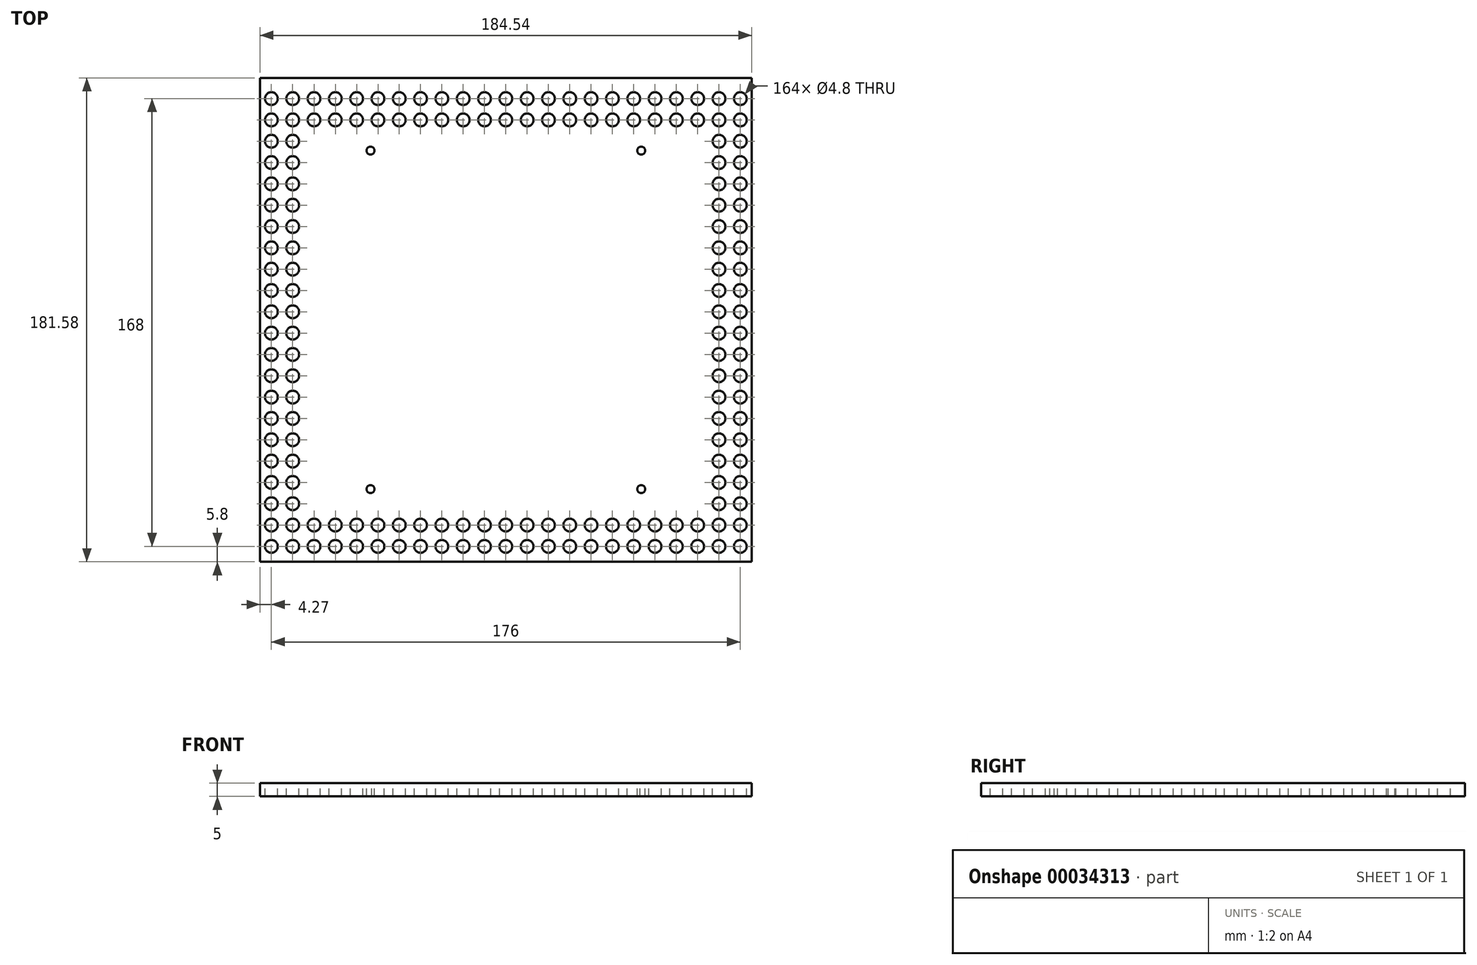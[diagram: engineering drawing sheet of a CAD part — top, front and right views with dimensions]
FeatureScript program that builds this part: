
annotation { "Feature Type Name" : "Feature", "Feature Type Description" : "" }
export const myFeature = defineFeature(function(context is Context, id is Id, definition is map)
    precondition{}
    {
        {
            var Q0;
            Q0=qCreatedBy(makeId("Top.planeOp"),FACE);
            var sketch = newSketch(context, id + "F0", { "sketchPlane" : qUnion([Q0])});
            skLineSegment(sketch, "E0.rect.bottom", {"start": v(92.28, 90.8) * mm, "end": v(-92.27, 90.8) * mm});
            skLineSegment(sketch, "E0.rect.top", {"start": v(92.27, -90.8) * mm, "end": v(-92.28, -90.8) * mm});
            skLineSegment(sketch, "E0.rect.left", {"start": v(92.28, 90.8) * mm, "end": v(92.27, -90.8) * mm});
            skLineSegment(sketch, "E0.rect.right", {"start": v(-92.27, 90.8) * mm, "end": v(-92.28, -90.8) * mm});
            skPoint(sketch, "E0.rect.middle", {"position": v(0, 0) * mm});
            skSolve(sketch);
        }
        {
            var Q0;
            Q0 = qSketchRegion(id + "F0", true);
            extrude(context, id + "F1", {"entities" : qUnion([Q0]), "depth" : 5 * mm});
        }
        {
            var Q0;
            Q0=makeQuery(id+"F1.opExtrude","CAP_FACE",FACE,{"disambiguationData":[OSD([sQuery(id+"F0.wireOp",EDGE,"E0.rect.bottom"),sQuery(id+"F0.wireOp",EDGE,"E0.rect.top"),sQuery(id+"F0.wireOp",EDGE,"E0.rect.left"),sQuery(id+"F0.wireOp",EDGE,"E0.rect.right")])],"isStart":false});
            var sketch = newSketch(context, id + "F2", { "sketchPlane" : qUnion([Q0])});
            skCircle(sketch, "E1", {"center": v(-88, -85) * mm, "radius": 2.4 * mm});
            skCircle(sketch, "E2.0.1.0", {"center": v(-88, -77) * mm, "radius": 2.4 * mm});
            skCircle(sketch, "E2.1.0.0", {"center": v(-80, -85) * mm, "radius": 2.4 * mm});
            skCircle(sketch, "E2.1.1.0", {"center": v(-80, -77) * mm, "radius": 2.4 * mm});
            skCircle(sketch, "E2.2.0.0", {"center": v(-72, -85) * mm, "radius": 2.4 * mm});
            skCircle(sketch, "E2.2.1.0", {"center": v(-72, -77) * mm, "radius": 2.4 * mm});
            skCircle(sketch, "E2.3.0.0", {"center": v(-64, -85) * mm, "radius": 2.4 * mm});
            skCircle(sketch, "E2.3.1.0", {"center": v(-64, -77) * mm, "radius": 2.4 * mm});
            skCircle(sketch, "E2.4.0.0", {"center": v(-56, -85) * mm, "radius": 2.4 * mm});
            skCircle(sketch, "E2.4.1.0", {"center": v(-56, -77) * mm, "radius": 2.4 * mm});
            skCircle(sketch, "E2.5.0.0", {"center": v(-48, -85) * mm, "radius": 2.4 * mm});
            skCircle(sketch, "E2.5.1.0", {"center": v(-48, -77) * mm, "radius": 2.4 * mm});
            skCircle(sketch, "E2.6.0.0", {"center": v(-40, -85) * mm, "radius": 2.4 * mm});
            skCircle(sketch, "E2.6.1.0", {"center": v(-40, -77) * mm, "radius": 2.4 * mm});
            skCircle(sketch, "E2.7.0.0", {"center": v(-32, -85) * mm, "radius": 2.4 * mm});
            skCircle(sketch, "E2.7.1.0", {"center": v(-32, -77) * mm, "radius": 2.4 * mm});
            skCircle(sketch, "E2.8.0.0", {"center": v(-24, -85) * mm, "radius": 2.4 * mm});
            skCircle(sketch, "E2.8.1.0", {"center": v(-24, -77) * mm, "radius": 2.4 * mm});
            skCircle(sketch, "E2.9.0.0", {"center": v(-16, -85) * mm, "radius": 2.4 * mm});
            skCircle(sketch, "E2.9.1.0", {"center": v(-16, -77) * mm, "radius": 2.4 * mm});
            skCircle(sketch, "E2.10.0.0", {"center": v(-8, -85) * mm, "radius": 2.4 * mm});
            skCircle(sketch, "E2.10.1.0", {"center": v(-8, -77) * mm, "radius": 2.4 * mm});
            skCircle(sketch, "E2.11.0.0", {"center": v(0, -85) * mm, "radius": 2.4 * mm});
            skCircle(sketch, "E2.11.1.0", {"center": v(0, -77) * mm, "radius": 2.4 * mm});
            skCircle(sketch, "E2.12.0.0", {"center": v(8, -85) * mm, "radius": 2.4 * mm});
            skCircle(sketch, "E2.12.1.0", {"center": v(8, -77) * mm, "radius": 2.4 * mm});
            skCircle(sketch, "E2.13.0.0", {"center": v(16, -85) * mm, "radius": 2.4 * mm});
            skCircle(sketch, "E2.13.1.0", {"center": v(16, -77) * mm, "radius": 2.4 * mm});
            skCircle(sketch, "E2.14.0.0", {"center": v(24, -85) * mm, "radius": 2.4 * mm});
            skCircle(sketch, "E2.14.1.0", {"center": v(24, -77) * mm, "radius": 2.4 * mm});
            skCircle(sketch, "E2.15.0.0", {"center": v(32, -85) * mm, "radius": 2.4 * mm});
            skCircle(sketch, "E2.15.1.0", {"center": v(32, -77) * mm, "radius": 2.4 * mm});
            skCircle(sketch, "E2.16.0.0", {"center": v(40, -85) * mm, "radius": 2.4 * mm});
            skCircle(sketch, "E2.16.1.0", {"center": v(40, -77) * mm, "radius": 2.4 * mm});
            skCircle(sketch, "E2.17.0.0", {"center": v(48, -85) * mm, "radius": 2.4 * mm});
            skCircle(sketch, "E2.17.1.0", {"center": v(48, -77) * mm, "radius": 2.4 * mm});
            skCircle(sketch, "E2.18.0.0", {"center": v(56, -85) * mm, "radius": 2.4 * mm});
            skCircle(sketch, "E2.18.1.0", {"center": v(56, -77) * mm, "radius": 2.4 * mm});
            skCircle(sketch, "E2.19.0.0", {"center": v(64, -85) * mm, "radius": 2.4 * mm});
            skCircle(sketch, "E2.19.1.0", {"center": v(64, -77) * mm, "radius": 2.4 * mm});
            skCircle(sketch, "E2.20.0.0", {"center": v(72, -85) * mm, "radius": 2.4 * mm});
            skCircle(sketch, "E2.20.1.0", {"center": v(72, -77) * mm, "radius": 2.4 * mm});
            skCircle(sketch, "E2.21.0.0", {"center": v(80, -85) * mm, "radius": 2.4 * mm});
            skCircle(sketch, "E2.21.1.0", {"center": v(80, -77) * mm, "radius": 2.4 * mm});
            skCircle(sketch, "E2.22.0.0", {"center": v(88, -85) * mm, "radius": 2.4 * mm});
            skCircle(sketch, "E2.22.1.0", {"center": v(88, -77) * mm, "radius": 2.4 * mm});
            skLineSegment(sketch, "E2.direction1", {"start": v(-88, -85) * mm, "end": v(-80, -85) * mm, "construction": true});
            skLineSegment(sketch, "E2.direction2", {"start": v(-88, -85) * mm, "end": v(-88, -77) * mm, "construction": true});
            skCircle(sketch, "E3.0.1.0", {"center": v(-88, -68.99) * mm, "radius": 2.4 * mm});
            skCircle(sketch, "E3.0.2.0", {"center": v(-88, -60.99) * mm, "radius": 2.4 * mm});
            skCircle(sketch, "E3.0.3.0", {"center": v(-88, -52.99) * mm, "radius": 2.4 * mm});
            skCircle(sketch, "E3.0.4.0", {"center": v(-88, -44.99) * mm, "radius": 2.4 * mm});
            skCircle(sketch, "E3.0.5.0", {"center": v(-88, -36.99) * mm, "radius": 2.4 * mm});
            skCircle(sketch, "E3.0.6.0", {"center": v(-88, -28.99) * mm, "radius": 2.4 * mm});
            skCircle(sketch, "E3.0.7.0", {"center": v(-88, -20.99) * mm, "radius": 2.4 * mm});
            skCircle(sketch, "E3.0.8.0", {"center": v(-88, -12.99) * mm, "radius": 2.4 * mm});
            skCircle(sketch, "E3.0.9.0", {"center": v(-88, -4.99) * mm, "radius": 2.4 * mm});
            skCircle(sketch, "E3.0.10.0", {"center": v(-88, 3.01) * mm, "radius": 2.4 * mm});
            skCircle(sketch, "E3.0.11.0", {"center": v(-88, 11.01) * mm, "radius": 2.4 * mm});
            skCircle(sketch, "E3.0.12.0", {"center": v(-88, 19.01) * mm, "radius": 2.4 * mm});
            skCircle(sketch, "E3.0.13.0", {"center": v(-88, 27.01) * mm, "radius": 2.4 * mm});
            skCircle(sketch, "E3.0.14.0", {"center": v(-88, 35.01) * mm, "radius": 2.4 * mm});
            skCircle(sketch, "E3.0.15.0", {"center": v(-88, 43.01) * mm, "radius": 2.4 * mm});
            skCircle(sketch, "E3.0.16.0", {"center": v(-88, 51.01) * mm, "radius": 2.4 * mm});
            skCircle(sketch, "E3.0.17.0", {"center": v(-88, 59.01) * mm, "radius": 2.4 * mm});
            skCircle(sketch, "E3.0.18.0", {"center": v(-88, 67.01) * mm, "radius": 2.4 * mm});
            skCircle(sketch, "E3.0.19.0", {"center": v(-88, 75.01) * mm, "radius": 2.4 * mm});
            skCircle(sketch, "E3.0.20.0", {"center": v(-88, 83.01) * mm, "radius": 2.4 * mm});
            skCircle(sketch, "E3.1.1.0", {"center": v(-80, -68.99) * mm, "radius": 2.4 * mm});
            skCircle(sketch, "E3.1.2.0", {"center": v(-80, -60.99) * mm, "radius": 2.4 * mm});
            skCircle(sketch, "E3.1.3.0", {"center": v(-80, -52.99) * mm, "radius": 2.4 * mm});
            skCircle(sketch, "E3.1.4.0", {"center": v(-80, -44.99) * mm, "radius": 2.4 * mm});
            skCircle(sketch, "E3.1.5.0", {"center": v(-80, -36.99) * mm, "radius": 2.4 * mm});
            skCircle(sketch, "E3.1.6.0", {"center": v(-80, -28.99) * mm, "radius": 2.4 * mm});
            skCircle(sketch, "E3.1.7.0", {"center": v(-80, -20.99) * mm, "radius": 2.4 * mm});
            skCircle(sketch, "E3.1.8.0", {"center": v(-80, -12.99) * mm, "radius": 2.4 * mm});
            skCircle(sketch, "E3.1.9.0", {"center": v(-80, -4.99) * mm, "radius": 2.4 * mm});
            skCircle(sketch, "E3.1.10.0", {"center": v(-80, 3.01) * mm, "radius": 2.4 * mm});
            skCircle(sketch, "E3.1.11.0", {"center": v(-80, 11.01) * mm, "radius": 2.4 * mm});
            skCircle(sketch, "E3.1.12.0", {"center": v(-80, 19.01) * mm, "radius": 2.4 * mm});
            skCircle(sketch, "E3.1.13.0", {"center": v(-80, 27.01) * mm, "radius": 2.4 * mm});
            skCircle(sketch, "E3.1.14.0", {"center": v(-80, 35.01) * mm, "radius": 2.4 * mm});
            skCircle(sketch, "E3.1.15.0", {"center": v(-80, 43.01) * mm, "radius": 2.4 * mm});
            skCircle(sketch, "E3.1.16.0", {"center": v(-80, 51.01) * mm, "radius": 2.4 * mm});
            skCircle(sketch, "E3.1.17.0", {"center": v(-80, 59.01) * mm, "radius": 2.4 * mm});
            skCircle(sketch, "E3.1.18.0", {"center": v(-80, 67.01) * mm, "radius": 2.4 * mm});
            skCircle(sketch, "E3.1.19.0", {"center": v(-80, 75.01) * mm, "radius": 2.4 * mm});
            skCircle(sketch, "E3.1.20.0", {"center": v(-80, 83.01) * mm, "radius": 2.4 * mm});
            skLineSegment(sketch, "E3.direction1", {"start": v(-88, -77) * mm, "end": v(-80, -77) * mm, "construction": true});
            skLineSegment(sketch, "E3.direction2", {"start": v(-88, -77) * mm, "end": v(-88, -68.99) * mm, "construction": true});
            skCircle(sketch, "E4.2.0.0", {"center": v(-72, 75.01) * mm, "radius": 2.4 * mm});
            skCircle(sketch, "E4.2.1.0", {"center": v(-72, 83.01) * mm, "radius": 2.4 * mm});
            skCircle(sketch, "E4.3.0.0", {"center": v(-64, 75.01) * mm, "radius": 2.4 * mm});
            skCircle(sketch, "E4.3.1.0", {"center": v(-64, 83.01) * mm, "radius": 2.4 * mm});
            skCircle(sketch, "E4.4.0.0", {"center": v(-56, 75.01) * mm, "radius": 2.4 * mm});
            skCircle(sketch, "E4.4.1.0", {"center": v(-56, 83.01) * mm, "radius": 2.4 * mm});
            skCircle(sketch, "E4.5.0.0", {"center": v(-48, 75.01) * mm, "radius": 2.4 * mm});
            skCircle(sketch, "E4.5.1.0", {"center": v(-48, 83.01) * mm, "radius": 2.4 * mm});
            skCircle(sketch, "E4.6.0.0", {"center": v(-40, 75.01) * mm, "radius": 2.4 * mm});
            skCircle(sketch, "E4.6.1.0", {"center": v(-40, 83.01) * mm, "radius": 2.4 * mm});
            skCircle(sketch, "E4.7.0.0", {"center": v(-32, 75.01) * mm, "radius": 2.4 * mm});
            skCircle(sketch, "E4.7.1.0", {"center": v(-32, 83.01) * mm, "radius": 2.4 * mm});
            skCircle(sketch, "E4.8.0.0", {"center": v(-24, 75.01) * mm, "radius": 2.4 * mm});
            skCircle(sketch, "E4.8.1.0", {"center": v(-24, 83.01) * mm, "radius": 2.4 * mm});
            skCircle(sketch, "E4.9.0.0", {"center": v(-16, 75.01) * mm, "radius": 2.4 * mm});
            skCircle(sketch, "E4.9.1.0", {"center": v(-16, 83.01) * mm, "radius": 2.4 * mm});
            skCircle(sketch, "E4.10.0.0", {"center": v(-8, 75.01) * mm, "radius": 2.4 * mm});
            skCircle(sketch, "E4.10.1.0", {"center": v(-8, 83.01) * mm, "radius": 2.4 * mm});
            skCircle(sketch, "E4.11.0.0", {"center": v(0, 75.01) * mm, "radius": 2.4 * mm});
            skCircle(sketch, "E4.11.1.0", {"center": v(0, 83.01) * mm, "radius": 2.4 * mm});
            skCircle(sketch, "E4.12.0.0", {"center": v(8, 75.01) * mm, "radius": 2.4 * mm});
            skCircle(sketch, "E4.12.1.0", {"center": v(8, 83.01) * mm, "radius": 2.4 * mm});
            skCircle(sketch, "E4.13.0.0", {"center": v(16, 75.01) * mm, "radius": 2.4 * mm});
            skCircle(sketch, "E4.13.1.0", {"center": v(16, 83.01) * mm, "radius": 2.4 * mm});
            skCircle(sketch, "E4.14.0.0", {"center": v(24, 75.01) * mm, "radius": 2.4 * mm});
            skCircle(sketch, "E4.14.1.0", {"center": v(24, 83.01) * mm, "radius": 2.4 * mm});
            skCircle(sketch, "E4.15.0.0", {"center": v(32, 75.01) * mm, "radius": 2.4 * mm});
            skCircle(sketch, "E4.15.1.0", {"center": v(32, 83.01) * mm, "radius": 2.4 * mm});
            skCircle(sketch, "E4.16.0.0", {"center": v(40, 75.01) * mm, "radius": 2.4 * mm});
            skCircle(sketch, "E4.16.1.0", {"center": v(40, 83.01) * mm, "radius": 2.4 * mm});
            skCircle(sketch, "E4.17.0.0", {"center": v(48, 75.01) * mm, "radius": 2.4 * mm});
            skCircle(sketch, "E4.17.1.0", {"center": v(48, 83.01) * mm, "radius": 2.4 * mm});
            skCircle(sketch, "E4.18.0.0", {"center": v(56, 75.01) * mm, "radius": 2.4 * mm});
            skCircle(sketch, "E4.18.1.0", {"center": v(56, 83.01) * mm, "radius": 2.4 * mm});
            skCircle(sketch, "E4.19.0.0", {"center": v(64, 75.01) * mm, "radius": 2.4 * mm});
            skCircle(sketch, "E4.19.1.0", {"center": v(64, 83.01) * mm, "radius": 2.4 * mm});
            skCircle(sketch, "E4.20.0.0", {"center": v(72, 75.01) * mm, "radius": 2.4 * mm});
            skCircle(sketch, "E4.20.1.0", {"center": v(72, 83.01) * mm, "radius": 2.4 * mm});
            skCircle(sketch, "E4.21.0.0", {"center": v(80, 75.01) * mm, "radius": 2.4 * mm});
            skCircle(sketch, "E4.21.1.0", {"center": v(80, 83.01) * mm, "radius": 2.4 * mm});
            skCircle(sketch, "E4.22.0.0", {"center": v(88, 75.01) * mm, "radius": 2.4 * mm});
            skCircle(sketch, "E4.22.1.0", {"center": v(88, 83.01) * mm, "radius": 2.4 * mm});
            skLineSegment(sketch, "E4.direction1", {"start": v(-88, 75.01) * mm, "end": v(-80, 75.01) * mm, "construction": true});
            skLineSegment(sketch, "E4.direction2", {"start": v(-88, 75.01) * mm, "end": v(-88, 83.01) * mm, "construction": true});
            skCircle(sketch, "E5.0.2.0", {"center": v(80, -68.99) * mm, "radius": 2.4 * mm});
            skCircle(sketch, "E5.0.3.0", {"center": v(80, -60.99) * mm, "radius": 2.4 * mm});
            skCircle(sketch, "E5.0.4.0", {"center": v(80, -52.99) * mm, "radius": 2.4 * mm});
            skCircle(sketch, "E5.0.5.0", {"center": v(80, -44.99) * mm, "radius": 2.4 * mm});
            skCircle(sketch, "E5.0.6.0", {"center": v(80, -36.99) * mm, "radius": 2.4 * mm});
            skCircle(sketch, "E5.0.7.0", {"center": v(80, -28.99) * mm, "radius": 2.4 * mm});
            skCircle(sketch, "E5.0.8.0", {"center": v(80, -20.99) * mm, "radius": 2.4 * mm});
            skCircle(sketch, "E5.0.9.0", {"center": v(80, -12.99) * mm, "radius": 2.4 * mm});
            skCircle(sketch, "E5.0.10.0", {"center": v(80, -4.99) * mm, "radius": 2.4 * mm});
            skCircle(sketch, "E5.0.11.0", {"center": v(80, 3.01) * mm, "radius": 2.4 * mm});
            skCircle(sketch, "E5.0.12.0", {"center": v(80, 11.01) * mm, "radius": 2.4 * mm});
            skCircle(sketch, "E5.0.13.0", {"center": v(80, 19.01) * mm, "radius": 2.4 * mm});
            skCircle(sketch, "E5.0.14.0", {"center": v(80, 27.01) * mm, "radius": 2.4 * mm});
            skCircle(sketch, "E5.0.15.0", {"center": v(80, 35.01) * mm, "radius": 2.4 * mm});
            skCircle(sketch, "E5.0.16.0", {"center": v(80, 43.01) * mm, "radius": 2.4 * mm});
            skCircle(sketch, "E5.0.17.0", {"center": v(80, 51.01) * mm, "radius": 2.4 * mm});
            skCircle(sketch, "E5.0.18.0", {"center": v(80, 59.01) * mm, "radius": 2.4 * mm});
            skCircle(sketch, "E5.0.19.0", {"center": v(80, 67.01) * mm, "radius": 2.4 * mm});
            skCircle(sketch, "E5.1.2.0", {"center": v(88, -68.99) * mm, "radius": 2.4 * mm});
            skCircle(sketch, "E5.1.3.0", {"center": v(88, -60.99) * mm, "radius": 2.4 * mm});
            skCircle(sketch, "E5.1.4.0", {"center": v(88, -52.99) * mm, "radius": 2.4 * mm});
            skCircle(sketch, "E5.1.5.0", {"center": v(88, -44.99) * mm, "radius": 2.4 * mm});
            skCircle(sketch, "E5.1.6.0", {"center": v(88, -36.99) * mm, "radius": 2.4 * mm});
            skCircle(sketch, "E5.1.7.0", {"center": v(88, -28.99) * mm, "radius": 2.4 * mm});
            skCircle(sketch, "E5.1.8.0", {"center": v(88, -20.99) * mm, "radius": 2.4 * mm});
            skCircle(sketch, "E5.1.9.0", {"center": v(88, -12.99) * mm, "radius": 2.4 * mm});
            skCircle(sketch, "E5.1.10.0", {"center": v(88, -4.99) * mm, "radius": 2.4 * mm});
            skCircle(sketch, "E5.1.11.0", {"center": v(88, 3.01) * mm, "radius": 2.4 * mm});
            skCircle(sketch, "E5.1.12.0", {"center": v(88, 11.01) * mm, "radius": 2.4 * mm});
            skCircle(sketch, "E5.1.13.0", {"center": v(88, 19.01) * mm, "radius": 2.4 * mm});
            skCircle(sketch, "E5.1.14.0", {"center": v(88, 27.01) * mm, "radius": 2.4 * mm});
            skCircle(sketch, "E5.1.15.0", {"center": v(88, 35.01) * mm, "radius": 2.4 * mm});
            skCircle(sketch, "E5.1.16.0", {"center": v(88, 43.01) * mm, "radius": 2.4 * mm});
            skCircle(sketch, "E5.1.17.0", {"center": v(88, 51.01) * mm, "radius": 2.4 * mm});
            skCircle(sketch, "E5.1.18.0", {"center": v(88, 59.01) * mm, "radius": 2.4 * mm});
            skCircle(sketch, "E5.1.19.0", {"center": v(88, 67.01) * mm, "radius": 2.4 * mm});
            skLineSegment(sketch, "E5.direction1", {"start": v(80, -85) * mm, "end": v(88, -85) * mm, "construction": true});
            skLineSegment(sketch, "E5.direction2", {"start": v(80, -85) * mm, "end": v(80, -77) * mm, "construction": true});
            skSolve(sketch);
        }
        {
            var Q0;
            Q0=makeQuery(id+"F2.imprint","IMPRINT",FACE,{"disambiguationData":[TD([[makeQuery(id+"F2.imprint","IMPRINT",EDGE,{"derivedFrom":sQuery(id+"F2.wireOp",EDGE,"E2.21.1.0")}),1.0]])]});
            var Q1;
            Q1=makeQuery(id+"F2.imprint","IMPRINT",FACE,{"disambiguationData":[TD([[makeQuery(id+"F2.imprint","IMPRINT",EDGE,{"derivedFrom":sQuery(id+"F2.wireOp",EDGE,"E2.22.1.0")}),1.0]])]});
            var Q2;
            Q2=makeQuery(id+"F2.imprint","IMPRINT",FACE,{"disambiguationData":[TD([[makeQuery(id+"F2.imprint","IMPRINT",EDGE,{"derivedFrom":sQuery(id+"F2.wireOp",EDGE,"E2.22.0.0")}),1.0]])]});
            var Q3;
            Q3=makeQuery(id+"F2.imprint","IMPRINT",FACE,{"disambiguationData":[TD([[makeQuery(id+"F2.imprint","IMPRINT",EDGE,{"derivedFrom":sQuery(id+"F2.wireOp",EDGE,"E2.21.0.0")}),1.0]])]});
            var Q4;
            Q4=makeQuery(id+"F2.imprint","IMPRINT",FACE,{"disambiguationData":[TD([[makeQuery(id+"F2.imprint","IMPRINT",EDGE,{"derivedFrom":sQuery(id+"F2.wireOp",EDGE,"E2.20.1.0")}),1.0]])]});
            var Q5;
            Q5=makeQuery(id+"F2.imprint","IMPRINT",FACE,{"disambiguationData":[TD([[makeQuery(id+"F2.imprint","IMPRINT",EDGE,{"derivedFrom":sQuery(id+"F2.wireOp",EDGE,"E2.20.0.0")}),1.0]])]});
            var Q6;
            Q6=makeQuery(id+"F2.imprint","IMPRINT",FACE,{"disambiguationData":[TD([[makeQuery(id+"F2.imprint","IMPRINT",EDGE,{"derivedFrom":sQuery(id+"F2.wireOp",EDGE,"E2.19.0.0")}),1.0]])]});
            var Q7;
            Q7=makeQuery(id+"F2.imprint","IMPRINT",FACE,{"disambiguationData":[TD([[makeQuery(id+"F2.imprint","IMPRINT",EDGE,{"derivedFrom":sQuery(id+"F2.wireOp",EDGE,"E2.19.1.0")}),1.0]])]});
            var Q8;
            Q8=makeQuery(id+"F2.imprint","IMPRINT",FACE,{"disambiguationData":[TD([[makeQuery(id+"F2.imprint","IMPRINT",EDGE,{"derivedFrom":sQuery(id+"F2.wireOp",EDGE,"E2.18.1.0")}),1.0]])]});
            var Q9;
            Q9=makeQuery(id+"F2.imprint","IMPRINT",FACE,{"disambiguationData":[TD([[makeQuery(id+"F2.imprint","IMPRINT",EDGE,{"derivedFrom":sQuery(id+"F2.wireOp",EDGE,"E2.18.0.0")}),1.0]])]});
            var Q10;
            Q10=makeQuery(id+"F2.imprint","IMPRINT",FACE,{"disambiguationData":[TD([[makeQuery(id+"F2.imprint","IMPRINT",EDGE,{"derivedFrom":sQuery(id+"F2.wireOp",EDGE,"E2.17.0.0")}),1.0]])]});
            var Q11;
            Q11=makeQuery(id+"F2.imprint","IMPRINT",FACE,{"disambiguationData":[TD([[makeQuery(id+"F2.imprint","IMPRINT",EDGE,{"derivedFrom":sQuery(id+"F2.wireOp",EDGE,"E2.17.1.0")}),1.0]])]});
            var Q12;
            Q12=makeQuery(id+"F2.imprint","IMPRINT",FACE,{"disambiguationData":[TD([[makeQuery(id+"F2.imprint","IMPRINT",EDGE,{"derivedFrom":sQuery(id+"F2.wireOp",EDGE,"E2.16.1.0")}),1.0]])]});
            var Q13;
            Q13=makeQuery(id+"F2.imprint","IMPRINT",FACE,{"disambiguationData":[TD([[makeQuery(id+"F2.imprint","IMPRINT",EDGE,{"derivedFrom":sQuery(id+"F2.wireOp",EDGE,"E2.16.0.0")}),1.0]])]});
            var Q14;
            Q14=makeQuery(id+"F2.imprint","IMPRINT",FACE,{"disambiguationData":[TD([[makeQuery(id+"F2.imprint","IMPRINT",EDGE,{"derivedFrom":sQuery(id+"F2.wireOp",EDGE,"E2.15.0.0")}),1.0]])]});
            var Q15;
            Q15=makeQuery(id+"F2.imprint","IMPRINT",FACE,{"disambiguationData":[TD([[makeQuery(id+"F2.imprint","IMPRINT",EDGE,{"derivedFrom":sQuery(id+"F2.wireOp",EDGE,"E2.15.1.0")}),1.0]])]});
            var Q16;
            Q16=makeQuery(id+"F2.imprint","IMPRINT",FACE,{"disambiguationData":[TD([[makeQuery(id+"F2.imprint","IMPRINT",EDGE,{"derivedFrom":sQuery(id+"F2.wireOp",EDGE,"E2.14.1.0")}),1.0]])]});
            var Q17;
            Q17=makeQuery(id+"F2.imprint","IMPRINT",FACE,{"disambiguationData":[TD([[makeQuery(id+"F2.imprint","IMPRINT",EDGE,{"derivedFrom":sQuery(id+"F2.wireOp",EDGE,"E2.14.0.0")}),1.0]])]});
            var Q18;
            Q18=makeQuery(id+"F2.imprint","IMPRINT",FACE,{"disambiguationData":[TD([[makeQuery(id+"F2.imprint","IMPRINT",EDGE,{"derivedFrom":sQuery(id+"F2.wireOp",EDGE,"E2.13.0.0")}),1.0]])]});
            var Q19;
            Q19=makeQuery(id+"F2.imprint","IMPRINT",FACE,{"disambiguationData":[TD([[makeQuery(id+"F2.imprint","IMPRINT",EDGE,{"derivedFrom":sQuery(id+"F2.wireOp",EDGE,"E2.13.1.0")}),1.0]])]});
            var Q20;
            Q20=makeQuery(id+"F2.imprint","IMPRINT",FACE,{"disambiguationData":[TD([[makeQuery(id+"F2.imprint","IMPRINT",EDGE,{"derivedFrom":sQuery(id+"F2.wireOp",EDGE,"E2.12.1.0")}),1.0]])]});
            var Q21;
            Q21=makeQuery(id+"F2.imprint","IMPRINT",FACE,{"disambiguationData":[TD([[makeQuery(id+"F2.imprint","IMPRINT",EDGE,{"derivedFrom":sQuery(id+"F2.wireOp",EDGE,"E2.12.0.0")}),1.0]])]});
            var Q22;
            Q22=makeQuery(id+"F2.imprint","IMPRINT",FACE,{"disambiguationData":[TD([[makeQuery(id+"F2.imprint","IMPRINT",EDGE,{"derivedFrom":sQuery(id+"F2.wireOp",EDGE,"E2.11.0.0")}),1.0]])]});
            var Q23;
            Q23=makeQuery(id+"F2.imprint","IMPRINT",FACE,{"disambiguationData":[TD([[makeQuery(id+"F2.imprint","IMPRINT",EDGE,{"derivedFrom":sQuery(id+"F2.wireOp",EDGE,"E2.11.1.0")}),1.0]])]});
            var Q24;
            Q24=makeQuery(id+"F2.imprint","IMPRINT",FACE,{"disambiguationData":[TD([[makeQuery(id+"F2.imprint","IMPRINT",EDGE,{"derivedFrom":sQuery(id+"F2.wireOp",EDGE,"E2.10.1.0")}),1.0]])]});
            var Q25;
            Q25=makeQuery(id+"F2.imprint","IMPRINT",FACE,{"disambiguationData":[TD([[makeQuery(id+"F2.imprint","IMPRINT",EDGE,{"derivedFrom":sQuery(id+"F2.wireOp",EDGE,"E2.10.0.0")}),1.0]])]});
            var Q26;
            Q26=makeQuery(id+"F2.imprint","IMPRINT",FACE,{"disambiguationData":[TD([[makeQuery(id+"F2.imprint","IMPRINT",EDGE,{"derivedFrom":sQuery(id+"F2.wireOp",EDGE,"E2.9.0.0")}),1.0]])]});
            var Q27;
            Q27=makeQuery(id+"F2.imprint","IMPRINT",FACE,{"disambiguationData":[TD([[makeQuery(id+"F2.imprint","IMPRINT",EDGE,{"derivedFrom":sQuery(id+"F2.wireOp",EDGE,"E2.9.1.0")}),1.0]])]});
            var Q28;
            Q28=makeQuery(id+"F2.imprint","IMPRINT",FACE,{"disambiguationData":[TD([[makeQuery(id+"F2.imprint","IMPRINT",EDGE,{"derivedFrom":sQuery(id+"F2.wireOp",EDGE,"E2.8.1.0")}),1.0]])]});
            var Q29;
            Q29=makeQuery(id+"F2.imprint","IMPRINT",FACE,{"disambiguationData":[TD([[makeQuery(id+"F2.imprint","IMPRINT",EDGE,{"derivedFrom":sQuery(id+"F2.wireOp",EDGE,"E2.8.0.0")}),1.0]])]});
            var Q30;
            Q30=makeQuery(id+"F2.imprint","IMPRINT",FACE,{"disambiguationData":[TD([[makeQuery(id+"F2.imprint","IMPRINT",EDGE,{"derivedFrom":sQuery(id+"F2.wireOp",EDGE,"E2.7.0.0")}),1.0]])]});
            var Q31;
            Q31=makeQuery(id+"F2.imprint","IMPRINT",FACE,{"disambiguationData":[TD([[makeQuery(id+"F2.imprint","IMPRINT",EDGE,{"derivedFrom":sQuery(id+"F2.wireOp",EDGE,"E2.7.1.0")}),1.0]])]});
            var Q32;
            Q32=makeQuery(id+"F2.imprint","IMPRINT",FACE,{"disambiguationData":[TD([[makeQuery(id+"F2.imprint","IMPRINT",EDGE,{"derivedFrom":sQuery(id+"F2.wireOp",EDGE,"E2.6.1.0")}),1.0]])]});
            var Q33;
            Q33=makeQuery(id+"F2.imprint","IMPRINT",FACE,{"disambiguationData":[TD([[makeQuery(id+"F2.imprint","IMPRINT",EDGE,{"derivedFrom":sQuery(id+"F2.wireOp",EDGE,"E2.6.0.0")}),1.0]])]});
            var Q34;
            Q34=makeQuery(id+"F2.imprint","IMPRINT",FACE,{"disambiguationData":[TD([[makeQuery(id+"F2.imprint","IMPRINT",EDGE,{"derivedFrom":sQuery(id+"F2.wireOp",EDGE,"E2.5.0.0")}),1.0]])]});
            var Q35;
            Q35=makeQuery(id+"F2.imprint","IMPRINT",FACE,{"disambiguationData":[TD([[makeQuery(id+"F2.imprint","IMPRINT",EDGE,{"derivedFrom":sQuery(id+"F2.wireOp",EDGE,"E2.5.1.0")}),1.0]])]});
            var Q36;
            Q36=makeQuery(id+"F2.imprint","IMPRINT",FACE,{"disambiguationData":[TD([[makeQuery(id+"F2.imprint","IMPRINT",EDGE,{"derivedFrom":sQuery(id+"F2.wireOp",EDGE,"E2.4.1.0")}),1.0]])]});
            var Q37;
            Q37=makeQuery(id+"F2.imprint","IMPRINT",FACE,{"disambiguationData":[TD([[makeQuery(id+"F2.imprint","IMPRINT",EDGE,{"derivedFrom":sQuery(id+"F2.wireOp",EDGE,"E2.4.0.0")}),1.0]])]});
            var Q38;
            Q38=makeQuery(id+"F2.imprint","IMPRINT",FACE,{"disambiguationData":[TD([[makeQuery(id+"F2.imprint","IMPRINT",EDGE,{"derivedFrom":sQuery(id+"F2.wireOp",EDGE,"E2.3.0.0")}),1.0]])]});
            var Q39;
            Q39=makeQuery(id+"F2.imprint","IMPRINT",FACE,{"disambiguationData":[TD([[makeQuery(id+"F2.imprint","IMPRINT",EDGE,{"derivedFrom":sQuery(id+"F2.wireOp",EDGE,"E2.2.0.0")}),1.0]])]});
            var Q40;
            Q40=makeQuery(id+"F2.imprint","IMPRINT",FACE,{"disambiguationData":[TD([[makeQuery(id+"F2.imprint","IMPRINT",EDGE,{"derivedFrom":sQuery(id+"F2.wireOp",EDGE,"E2.2.1.0")}),1.0]])]});
            var Q41;
            Q41=makeQuery(id+"F2.imprint","IMPRINT",FACE,{"disambiguationData":[TD([[makeQuery(id+"F2.imprint","IMPRINT",EDGE,{"derivedFrom":sQuery(id+"F2.wireOp",EDGE,"E2.3.1.0")}),1.0]])]});
            var Q42;
            Q42=makeQuery(id+"F2.imprint","IMPRINT",FACE,{"disambiguationData":[TD([[makeQuery(id+"F2.imprint","IMPRINT",EDGE,{"derivedFrom":sQuery(id+"F2.wireOp",EDGE,"E2.1.0.0")}),1.0]])]});
            var Q43;
            Q43=makeQuery(id+"F2.imprint","IMPRINT",FACE,{"disambiguationData":[TD([[makeQuery(id+"F2.imprint","IMPRINT",EDGE,{"derivedFrom":sQuery(id+"F2.wireOp",EDGE,"E1")}),1.0]])]});
            var Q44;
            Q44=makeQuery(id+"F2.imprint","IMPRINT",FACE,{"disambiguationData":[TD([[makeQuery(id+"F2.imprint","IMPRINT",EDGE,{"derivedFrom":sQuery(id+"F2.wireOp",EDGE,"E2.0.1.0")}),1.0]])]});
            var Q45;
            Q45=makeQuery(id+"F2.imprint","IMPRINT",FACE,{"disambiguationData":[TD([[makeQuery(id+"F2.imprint","IMPRINT",EDGE,{"derivedFrom":sQuery(id+"F2.wireOp",EDGE,"E2.1.1.0")}),1.0]])]});
            var Q46;
            Q46=makeQuery(id+"F2.imprint","IMPRINT",FACE,{"disambiguationData":[TD([[makeQuery(id+"F2.imprint","IMPRINT",EDGE,{"derivedFrom":sQuery(id+"F2.wireOp",EDGE,"E3.1.1.0")}),1.0]])]});
            var Q47;
            Q47=makeQuery(id+"F2.imprint","IMPRINT",FACE,{"disambiguationData":[TD([[makeQuery(id+"F2.imprint","IMPRINT",EDGE,{"derivedFrom":sQuery(id+"F2.wireOp",EDGE,"E3.0.1.0")}),1.0]])]});
            var Q48;
            Q48=makeQuery(id+"F2.imprint","IMPRINT",FACE,{"disambiguationData":[TD([[makeQuery(id+"F2.imprint","IMPRINT",EDGE,{"derivedFrom":sQuery(id+"F2.wireOp",EDGE,"E3.0.2.0")}),1.0]])]});
            var Q49;
            Q49=makeQuery(id+"F2.imprint","IMPRINT",FACE,{"disambiguationData":[TD([[makeQuery(id+"F2.imprint","IMPRINT",EDGE,{"derivedFrom":sQuery(id+"F2.wireOp",EDGE,"E3.1.2.0")}),1.0]])]});
            var Q50;
            Q50=makeQuery(id+"F2.imprint","IMPRINT",FACE,{"disambiguationData":[TD([[makeQuery(id+"F2.imprint","IMPRINT",EDGE,{"derivedFrom":sQuery(id+"F2.wireOp",EDGE,"E3.1.3.0")}),1.0]])]});
            var Q51;
            Q51=makeQuery(id+"F2.imprint","IMPRINT",FACE,{"disambiguationData":[TD([[makeQuery(id+"F2.imprint","IMPRINT",EDGE,{"derivedFrom":sQuery(id+"F2.wireOp",EDGE,"E3.0.3.0")}),1.0]])]});
            var Q52;
            Q52=makeQuery(id+"F2.imprint","IMPRINT",FACE,{"disambiguationData":[TD([[makeQuery(id+"F2.imprint","IMPRINT",EDGE,{"derivedFrom":sQuery(id+"F2.wireOp",EDGE,"E3.0.4.0")}),1.0]])]});
            var Q53;
            Q53=makeQuery(id+"F2.imprint","IMPRINT",FACE,{"disambiguationData":[TD([[makeQuery(id+"F2.imprint","IMPRINT",EDGE,{"derivedFrom":sQuery(id+"F2.wireOp",EDGE,"E3.1.4.0")}),1.0]])]});
            var Q54;
            Q54=makeQuery(id+"F2.imprint","IMPRINT",FACE,{"disambiguationData":[TD([[makeQuery(id+"F2.imprint","IMPRINT",EDGE,{"derivedFrom":sQuery(id+"F2.wireOp",EDGE,"E3.1.5.0")}),1.0]])]});
            var Q55;
            Q55=makeQuery(id+"F2.imprint","IMPRINT",FACE,{"disambiguationData":[TD([[makeQuery(id+"F2.imprint","IMPRINT",EDGE,{"derivedFrom":sQuery(id+"F2.wireOp",EDGE,"E3.0.5.0")}),1.0]])]});
            var Q56;
            Q56=makeQuery(id+"F2.imprint","IMPRINT",FACE,{"disambiguationData":[TD([[makeQuery(id+"F2.imprint","IMPRINT",EDGE,{"derivedFrom":sQuery(id+"F2.wireOp",EDGE,"E3.0.6.0")}),1.0]])]});
            var Q57;
            Q57=makeQuery(id+"F2.imprint","IMPRINT",FACE,{"disambiguationData":[TD([[makeQuery(id+"F2.imprint","IMPRINT",EDGE,{"derivedFrom":sQuery(id+"F2.wireOp",EDGE,"E3.1.6.0")}),1.0]])]});
            var Q58;
            Q58=makeQuery(id+"F2.imprint","IMPRINT",FACE,{"disambiguationData":[TD([[makeQuery(id+"F2.imprint","IMPRINT",EDGE,{"derivedFrom":sQuery(id+"F2.wireOp",EDGE,"E3.1.7.0")}),1.0]])]});
            var Q59;
            Q59=makeQuery(id+"F2.imprint","IMPRINT",FACE,{"disambiguationData":[TD([[makeQuery(id+"F2.imprint","IMPRINT",EDGE,{"derivedFrom":sQuery(id+"F2.wireOp",EDGE,"E3.0.7.0")}),1.0]])]});
            var Q60;
            Q60=makeQuery(id+"F2.imprint","IMPRINT",FACE,{"disambiguationData":[TD([[makeQuery(id+"F2.imprint","IMPRINT",EDGE,{"derivedFrom":sQuery(id+"F2.wireOp",EDGE,"E3.0.8.0")}),1.0]])]});
            var Q61;
            Q61=makeQuery(id+"F2.imprint","IMPRINT",FACE,{"disambiguationData":[TD([[makeQuery(id+"F2.imprint","IMPRINT",EDGE,{"derivedFrom":sQuery(id+"F2.wireOp",EDGE,"E3.1.8.0")}),1.0]])]});
            var Q62;
            Q62=makeQuery(id+"F2.imprint","IMPRINT",FACE,{"disambiguationData":[TD([[makeQuery(id+"F2.imprint","IMPRINT",EDGE,{"derivedFrom":sQuery(id+"F2.wireOp",EDGE,"E3.1.9.0")}),1.0]])]});
            var Q63;
            Q63=makeQuery(id+"F2.imprint","IMPRINT",FACE,{"disambiguationData":[TD([[makeQuery(id+"F2.imprint","IMPRINT",EDGE,{"derivedFrom":sQuery(id+"F2.wireOp",EDGE,"E3.0.9.0")}),1.0]])]});
            var Q64;
            Q64=makeQuery(id+"F2.imprint","IMPRINT",FACE,{"disambiguationData":[TD([[makeQuery(id+"F2.imprint","IMPRINT",EDGE,{"derivedFrom":sQuery(id+"F2.wireOp",EDGE,"E3.0.10.0")}),1.0]])]});
            var Q65;
            Q65=makeQuery(id+"F2.imprint","IMPRINT",FACE,{"disambiguationData":[TD([[makeQuery(id+"F2.imprint","IMPRINT",EDGE,{"derivedFrom":sQuery(id+"F2.wireOp",EDGE,"E3.1.10.0")}),1.0]])]});
            var Q66;
            Q66=makeQuery(id+"F2.imprint","IMPRINT",FACE,{"disambiguationData":[TD([[makeQuery(id+"F2.imprint","IMPRINT",EDGE,{"derivedFrom":sQuery(id+"F2.wireOp",EDGE,"E3.1.11.0")}),1.0]])]});
            var Q67;
            Q67=makeQuery(id+"F2.imprint","IMPRINT",FACE,{"disambiguationData":[TD([[makeQuery(id+"F2.imprint","IMPRINT",EDGE,{"derivedFrom":sQuery(id+"F2.wireOp",EDGE,"E3.0.11.0")}),1.0]])]});
            var Q68;
            Q68=makeQuery(id+"F2.imprint","IMPRINT",FACE,{"disambiguationData":[TD([[makeQuery(id+"F2.imprint","IMPRINT",EDGE,{"derivedFrom":sQuery(id+"F2.wireOp",EDGE,"E3.0.12.0")}),1.0]])]});
            var Q69;
            Q69=makeQuery(id+"F2.imprint","IMPRINT",FACE,{"disambiguationData":[TD([[makeQuery(id+"F2.imprint","IMPRINT",EDGE,{"derivedFrom":sQuery(id+"F2.wireOp",EDGE,"E3.1.12.0")}),1.0]])]});
            var Q70;
            Q70=makeQuery(id+"F2.imprint","IMPRINT",FACE,{"disambiguationData":[TD([[makeQuery(id+"F2.imprint","IMPRINT",EDGE,{"derivedFrom":sQuery(id+"F2.wireOp",EDGE,"E3.0.13.0")}),1.0]])]});
            var Q71;
            Q71=makeQuery(id+"F2.imprint","IMPRINT",FACE,{"disambiguationData":[TD([[makeQuery(id+"F2.imprint","IMPRINT",EDGE,{"derivedFrom":sQuery(id+"F2.wireOp",EDGE,"E3.1.13.0")}),1.0]])]});
            var Q72;
            Q72=makeQuery(id+"F2.imprint","IMPRINT",FACE,{"disambiguationData":[TD([[makeQuery(id+"F2.imprint","IMPRINT",EDGE,{"derivedFrom":sQuery(id+"F2.wireOp",EDGE,"E3.1.14.0")}),1.0]])]});
            var Q73;
            Q73=makeQuery(id+"F2.imprint","IMPRINT",FACE,{"disambiguationData":[TD([[makeQuery(id+"F2.imprint","IMPRINT",EDGE,{"derivedFrom":sQuery(id+"F2.wireOp",EDGE,"E3.0.14.0")}),1.0]])]});
            var Q74;
            Q74=makeQuery(id+"F2.imprint","IMPRINT",FACE,{"disambiguationData":[TD([[makeQuery(id+"F2.imprint","IMPRINT",EDGE,{"derivedFrom":sQuery(id+"F2.wireOp",EDGE,"E3.0.15.0")}),1.0]])]});
            var Q75;
            Q75=makeQuery(id+"F2.imprint","IMPRINT",FACE,{"disambiguationData":[TD([[makeQuery(id+"F2.imprint","IMPRINT",EDGE,{"derivedFrom":sQuery(id+"F2.wireOp",EDGE,"E3.1.15.0")}),1.0]])]});
            var Q76;
            Q76=makeQuery(id+"F2.imprint","IMPRINT",FACE,{"disambiguationData":[TD([[makeQuery(id+"F2.imprint","IMPRINT",EDGE,{"derivedFrom":sQuery(id+"F2.wireOp",EDGE,"E3.1.16.0")}),1.0]])]});
            var Q77;
            Q77=makeQuery(id+"F2.imprint","IMPRINT",FACE,{"disambiguationData":[TD([[makeQuery(id+"F2.imprint","IMPRINT",EDGE,{"derivedFrom":sQuery(id+"F2.wireOp",EDGE,"E3.0.16.0")}),1.0]])]});
            var Q78;
            Q78=makeQuery(id+"F2.imprint","IMPRINT",FACE,{"disambiguationData":[TD([[makeQuery(id+"F2.imprint","IMPRINT",EDGE,{"derivedFrom":sQuery(id+"F2.wireOp",EDGE,"E3.0.17.0")}),1.0]])]});
            var Q79;
            Q79=makeQuery(id+"F2.imprint","IMPRINT",FACE,{"disambiguationData":[TD([[makeQuery(id+"F2.imprint","IMPRINT",EDGE,{"derivedFrom":sQuery(id+"F2.wireOp",EDGE,"E3.1.17.0")}),1.0]])]});
            var Q80;
            Q80=makeQuery(id+"F2.imprint","IMPRINT",FACE,{"disambiguationData":[TD([[makeQuery(id+"F2.imprint","IMPRINT",EDGE,{"derivedFrom":sQuery(id+"F2.wireOp",EDGE,"E3.1.18.0")}),1.0]])]});
            var Q81;
            Q81=makeQuery(id+"F2.imprint","IMPRINT",FACE,{"disambiguationData":[TD([[makeQuery(id+"F2.imprint","IMPRINT",EDGE,{"derivedFrom":sQuery(id+"F2.wireOp",EDGE,"E3.0.18.0")}),1.0]])]});
            var Q82;
            Q82=makeQuery(id+"F2.imprint","IMPRINT",FACE,{"disambiguationData":[TD([[makeQuery(id+"F2.imprint","IMPRINT",EDGE,{"derivedFrom":sQuery(id+"F2.wireOp",EDGE,"E3.0.19.0")}),1.0]])]});
            var Q83;
            Q83=makeQuery(id+"F2.imprint","IMPRINT",FACE,{"disambiguationData":[TD([[makeQuery(id+"F2.imprint","IMPRINT",EDGE,{"derivedFrom":sQuery(id+"F2.wireOp",EDGE,"E3.0.20.0")}),1.0]])]});
            var Q84;
            Q84=makeQuery(id+"F2.imprint","IMPRINT",FACE,{"disambiguationData":[TD([[makeQuery(id+"F2.imprint","IMPRINT",EDGE,{"derivedFrom":sQuery(id+"F2.wireOp",EDGE,"E3.1.20.0")}),1.0]])]});
            var Q85;
            Q85=makeQuery(id+"F2.imprint","IMPRINT",FACE,{"disambiguationData":[TD([[makeQuery(id+"F2.imprint","IMPRINT",EDGE,{"derivedFrom":sQuery(id+"F2.wireOp",EDGE,"E3.1.19.0")}),1.0]])]});
            var Q86;
            Q86=makeQuery(id+"F2.imprint","IMPRINT",FACE,{"disambiguationData":[TD([[makeQuery(id+"F2.imprint","IMPRINT",EDGE,{"derivedFrom":sQuery(id+"F2.wireOp",EDGE,"E4.2.0.0")}),1.0]])]});
            var Q87;
            Q87=makeQuery(id+"F2.imprint","IMPRINT",FACE,{"disambiguationData":[TD([[makeQuery(id+"F2.imprint","IMPRINT",EDGE,{"derivedFrom":sQuery(id+"F2.wireOp",EDGE,"E4.2.1.0")}),1.0]])]});
            var Q88;
            Q88=makeQuery(id+"F2.imprint","IMPRINT",FACE,{"disambiguationData":[TD([[makeQuery(id+"F2.imprint","IMPRINT",EDGE,{"derivedFrom":sQuery(id+"F2.wireOp",EDGE,"E4.3.1.0")}),1.0]])]});
            var Q89;
            Q89=makeQuery(id+"F2.imprint","IMPRINT",FACE,{"disambiguationData":[TD([[makeQuery(id+"F2.imprint","IMPRINT",EDGE,{"derivedFrom":sQuery(id+"F2.wireOp",EDGE,"E4.3.0.0")}),1.0]])]});
            var Q90;
            Q90=makeQuery(id+"F2.imprint","IMPRINT",FACE,{"disambiguationData":[TD([[makeQuery(id+"F2.imprint","IMPRINT",EDGE,{"derivedFrom":sQuery(id+"F2.wireOp",EDGE,"E4.4.0.0")}),1.0]])]});
            var Q91;
            Q91=makeQuery(id+"F2.imprint","IMPRINT",FACE,{"disambiguationData":[TD([[makeQuery(id+"F2.imprint","IMPRINT",EDGE,{"derivedFrom":sQuery(id+"F2.wireOp",EDGE,"E4.4.1.0")}),1.0]])]});
            var Q92;
            Q92=makeQuery(id+"F2.imprint","IMPRINT",FACE,{"disambiguationData":[TD([[makeQuery(id+"F2.imprint","IMPRINT",EDGE,{"derivedFrom":sQuery(id+"F2.wireOp",EDGE,"E4.5.1.0")}),1.0]])]});
            var Q93;
            Q93=makeQuery(id+"F2.imprint","IMPRINT",FACE,{"disambiguationData":[TD([[makeQuery(id+"F2.imprint","IMPRINT",EDGE,{"derivedFrom":sQuery(id+"F2.wireOp",EDGE,"E4.5.0.0")}),1.0]])]});
            var Q94;
            Q94=makeQuery(id+"F2.imprint","IMPRINT",FACE,{"disambiguationData":[TD([[makeQuery(id+"F2.imprint","IMPRINT",EDGE,{"derivedFrom":sQuery(id+"F2.wireOp",EDGE,"E4.6.0.0")}),1.0]])]});
            var Q95;
            Q95=makeQuery(id+"F2.imprint","IMPRINT",FACE,{"disambiguationData":[TD([[makeQuery(id+"F2.imprint","IMPRINT",EDGE,{"derivedFrom":sQuery(id+"F2.wireOp",EDGE,"E4.6.1.0")}),1.0]])]});
            var Q96;
            Q96=makeQuery(id+"F2.imprint","IMPRINT",FACE,{"disambiguationData":[TD([[makeQuery(id+"F2.imprint","IMPRINT",EDGE,{"derivedFrom":sQuery(id+"F2.wireOp",EDGE,"E4.7.1.0")}),1.0]])]});
            var Q97;
            Q97=makeQuery(id+"F2.imprint","IMPRINT",FACE,{"disambiguationData":[TD([[makeQuery(id+"F2.imprint","IMPRINT",EDGE,{"derivedFrom":sQuery(id+"F2.wireOp",EDGE,"E4.7.0.0")}),1.0]])]});
            var Q98;
            Q98=makeQuery(id+"F2.imprint","IMPRINT",FACE,{"disambiguationData":[TD([[makeQuery(id+"F2.imprint","IMPRINT",EDGE,{"derivedFrom":sQuery(id+"F2.wireOp",EDGE,"E4.8.0.0")}),1.0]])]});
            var Q99;
            Q99=makeQuery(id+"F2.imprint","IMPRINT",FACE,{"disambiguationData":[TD([[makeQuery(id+"F2.imprint","IMPRINT",EDGE,{"derivedFrom":sQuery(id+"F2.wireOp",EDGE,"E4.8.1.0")}),1.0]])]});
            var Q100;
            Q100=makeQuery(id+"F2.imprint","IMPRINT",FACE,{"disambiguationData":[TD([[makeQuery(id+"F2.imprint","IMPRINT",EDGE,{"derivedFrom":sQuery(id+"F2.wireOp",EDGE,"E4.9.1.0")}),1.0]])]});
            var Q101;
            Q101=makeQuery(id+"F2.imprint","IMPRINT",FACE,{"disambiguationData":[TD([[makeQuery(id+"F2.imprint","IMPRINT",EDGE,{"derivedFrom":sQuery(id+"F2.wireOp",EDGE,"E4.9.0.0")}),1.0]])]});
            var Q102;
            Q102=makeQuery(id+"F2.imprint","IMPRINT",FACE,{"disambiguationData":[TD([[makeQuery(id+"F2.imprint","IMPRINT",EDGE,{"derivedFrom":sQuery(id+"F2.wireOp",EDGE,"E4.10.1.0")}),1.0]])]});
            var Q103;
            Q103=makeQuery(id+"F2.imprint","IMPRINT",FACE,{"disambiguationData":[TD([[makeQuery(id+"F2.imprint","IMPRINT",EDGE,{"derivedFrom":sQuery(id+"F2.wireOp",EDGE,"E4.10.0.0")}),1.0]])]});
            var Q104;
            Q104=makeQuery(id+"F2.imprint","IMPRINT",FACE,{"disambiguationData":[TD([[makeQuery(id+"F2.imprint","IMPRINT",EDGE,{"derivedFrom":sQuery(id+"F2.wireOp",EDGE,"E4.11.1.0")}),1.0]])]});
            var Q105;
            Q105=makeQuery(id+"F2.imprint","IMPRINT",FACE,{"disambiguationData":[TD([[makeQuery(id+"F2.imprint","IMPRINT",EDGE,{"derivedFrom":sQuery(id+"F2.wireOp",EDGE,"E4.11.0.0")}),1.0]])]});
            var Q106;
            Q106=makeQuery(id+"F2.imprint","IMPRINT",FACE,{"disambiguationData":[TD([[makeQuery(id+"F2.imprint","IMPRINT",EDGE,{"derivedFrom":sQuery(id+"F2.wireOp",EDGE,"E4.12.1.0")}),1.0]])]});
            var Q107;
            Q107=makeQuery(id+"F2.imprint","IMPRINT",FACE,{"disambiguationData":[TD([[makeQuery(id+"F2.imprint","IMPRINT",EDGE,{"derivedFrom":sQuery(id+"F2.wireOp",EDGE,"E4.12.0.0")}),1.0]])]});
            var Q108;
            Q108=makeQuery(id+"F2.imprint","IMPRINT",FACE,{"disambiguationData":[TD([[makeQuery(id+"F2.imprint","IMPRINT",EDGE,{"derivedFrom":sQuery(id+"F2.wireOp",EDGE,"E4.13.0.0")}),1.0]])]});
            var Q109;
            Q109=makeQuery(id+"F2.imprint","IMPRINT",FACE,{"disambiguationData":[TD([[makeQuery(id+"F2.imprint","IMPRINT",EDGE,{"derivedFrom":sQuery(id+"F2.wireOp",EDGE,"E4.13.1.0")}),1.0]])]});
            var Q110;
            Q110=makeQuery(id+"F2.imprint","IMPRINT",FACE,{"disambiguationData":[TD([[makeQuery(id+"F2.imprint","IMPRINT",EDGE,{"derivedFrom":sQuery(id+"F2.wireOp",EDGE,"E4.14.1.0")}),1.0]])]});
            var Q111;
            Q111=makeQuery(id+"F2.imprint","IMPRINT",FACE,{"disambiguationData":[TD([[makeQuery(id+"F2.imprint","IMPRINT",EDGE,{"derivedFrom":sQuery(id+"F2.wireOp",EDGE,"E4.14.0.0")}),1.0]])]});
            var Q112;
            Q112=makeQuery(id+"F2.imprint","IMPRINT",FACE,{"disambiguationData":[TD([[makeQuery(id+"F2.imprint","IMPRINT",EDGE,{"derivedFrom":sQuery(id+"F2.wireOp",EDGE,"E4.15.0.0")}),1.0]])]});
            var Q113;
            Q113=makeQuery(id+"F2.imprint","IMPRINT",FACE,{"disambiguationData":[TD([[makeQuery(id+"F2.imprint","IMPRINT",EDGE,{"derivedFrom":sQuery(id+"F2.wireOp",EDGE,"E4.15.1.0")}),1.0]])]});
            var Q114;
            Q114=makeQuery(id+"F2.imprint","IMPRINT",FACE,{"disambiguationData":[TD([[makeQuery(id+"F2.imprint","IMPRINT",EDGE,{"derivedFrom":sQuery(id+"F2.wireOp",EDGE,"E4.16.1.0")}),1.0]])]});
            var Q115;
            Q115=makeQuery(id+"F2.imprint","IMPRINT",FACE,{"disambiguationData":[TD([[makeQuery(id+"F2.imprint","IMPRINT",EDGE,{"derivedFrom":sQuery(id+"F2.wireOp",EDGE,"E4.16.0.0")}),1.0]])]});
            var Q116;
            Q116=makeQuery(id+"F2.imprint","IMPRINT",FACE,{"disambiguationData":[TD([[makeQuery(id+"F2.imprint","IMPRINT",EDGE,{"derivedFrom":sQuery(id+"F2.wireOp",EDGE,"E4.17.0.0")}),1.0]])]});
            var Q117;
            Q117=makeQuery(id+"F2.imprint","IMPRINT",FACE,{"disambiguationData":[TD([[makeQuery(id+"F2.imprint","IMPRINT",EDGE,{"derivedFrom":sQuery(id+"F2.wireOp",EDGE,"E4.17.1.0")}),1.0]])]});
            var Q118;
            Q118=makeQuery(id+"F2.imprint","IMPRINT",FACE,{"disambiguationData":[TD([[makeQuery(id+"F2.imprint","IMPRINT",EDGE,{"derivedFrom":sQuery(id+"F2.wireOp",EDGE,"E4.18.1.0")}),1.0]])]});
            var Q119;
            Q119=makeQuery(id+"F2.imprint","IMPRINT",FACE,{"disambiguationData":[TD([[makeQuery(id+"F2.imprint","IMPRINT",EDGE,{"derivedFrom":sQuery(id+"F2.wireOp",EDGE,"E4.18.0.0")}),1.0]])]});
            var Q120;
            Q120=makeQuery(id+"F2.imprint","IMPRINT",FACE,{"disambiguationData":[TD([[makeQuery(id+"F2.imprint","IMPRINT",EDGE,{"derivedFrom":sQuery(id+"F2.wireOp",EDGE,"E4.19.0.0")}),1.0]])]});
            var Q121;
            Q121=makeQuery(id+"F2.imprint","IMPRINT",FACE,{"disambiguationData":[TD([[makeQuery(id+"F2.imprint","IMPRINT",EDGE,{"derivedFrom":sQuery(id+"F2.wireOp",EDGE,"E4.19.1.0")}),1.0]])]});
            var Q122;
            Q122=makeQuery(id+"F2.imprint","IMPRINT",FACE,{"disambiguationData":[TD([[makeQuery(id+"F2.imprint","IMPRINT",EDGE,{"derivedFrom":sQuery(id+"F2.wireOp",EDGE,"E4.20.1.0")}),1.0]])]});
            var Q123;
            Q123=makeQuery(id+"F2.imprint","IMPRINT",FACE,{"disambiguationData":[TD([[makeQuery(id+"F2.imprint","IMPRINT",EDGE,{"derivedFrom":sQuery(id+"F2.wireOp",EDGE,"E4.20.0.0")}),1.0]])]});
            var Q124;
            Q124=makeQuery(id+"F2.imprint","IMPRINT",FACE,{"disambiguationData":[TD([[makeQuery(id+"F2.imprint","IMPRINT",EDGE,{"derivedFrom":sQuery(id+"F2.wireOp",EDGE,"E4.21.1.0")}),1.0]])]});
            var Q125;
            Q125=makeQuery(id+"F2.imprint","IMPRINT",FACE,{"disambiguationData":[TD([[makeQuery(id+"F2.imprint","IMPRINT",EDGE,{"derivedFrom":sQuery(id+"F2.wireOp",EDGE,"E4.22.1.0")}),1.0]])]});
            var Q126;
            Q126=makeQuery(id+"F2.imprint","IMPRINT",FACE,{"disambiguationData":[TD([[makeQuery(id+"F2.imprint","IMPRINT",EDGE,{"derivedFrom":sQuery(id+"F2.wireOp",EDGE,"E4.22.0.0")}),1.0]])]});
            var Q127;
            Q127=makeQuery(id+"F2.imprint","IMPRINT",FACE,{"disambiguationData":[TD([[makeQuery(id+"F2.imprint","IMPRINT",EDGE,{"derivedFrom":sQuery(id+"F2.wireOp",EDGE,"E4.21.0.0")}),1.0]])]});
            var Q128;
            Q128=makeQuery(id+"F2.imprint","IMPRINT",FACE,{"disambiguationData":[TD([[makeQuery(id+"F2.imprint","IMPRINT",EDGE,{"derivedFrom":sQuery(id+"F2.wireOp",EDGE,"E5.0.19.0")}),1.0]])]});
            var Q129;
            Q129=makeQuery(id+"F2.imprint","IMPRINT",FACE,{"disambiguationData":[TD([[makeQuery(id+"F2.imprint","IMPRINT",EDGE,{"derivedFrom":sQuery(id+"F2.wireOp",EDGE,"E5.1.19.0")}),1.0]])]});
            var Q130;
            Q130=makeQuery(id+"F2.imprint","IMPRINT",FACE,{"disambiguationData":[TD([[makeQuery(id+"F2.imprint","IMPRINT",EDGE,{"derivedFrom":sQuery(id+"F2.wireOp",EDGE,"E5.1.18.0")}),1.0]])]});
            var Q131;
            Q131=makeQuery(id+"F2.imprint","IMPRINT",FACE,{"disambiguationData":[TD([[makeQuery(id+"F2.imprint","IMPRINT",EDGE,{"derivedFrom":sQuery(id+"F2.wireOp",EDGE,"E5.0.18.0")}),1.0]])]});
            var Q132;
            Q132=makeQuery(id+"F2.imprint","IMPRINT",FACE,{"disambiguationData":[TD([[makeQuery(id+"F2.imprint","IMPRINT",EDGE,{"derivedFrom":sQuery(id+"F2.wireOp",EDGE,"E5.0.17.0")}),1.0]])]});
            var Q133;
            Q133=makeQuery(id+"F2.imprint","IMPRINT",FACE,{"disambiguationData":[TD([[makeQuery(id+"F2.imprint","IMPRINT",EDGE,{"derivedFrom":sQuery(id+"F2.wireOp",EDGE,"E5.1.17.0")}),1.0]])]});
            var Q134;
            Q134=makeQuery(id+"F2.imprint","IMPRINT",FACE,{"disambiguationData":[TD([[makeQuery(id+"F2.imprint","IMPRINT",EDGE,{"derivedFrom":sQuery(id+"F2.wireOp",EDGE,"E5.1.16.0")}),1.0]])]});
            var Q135;
            Q135=makeQuery(id+"F2.imprint","IMPRINT",FACE,{"disambiguationData":[TD([[makeQuery(id+"F2.imprint","IMPRINT",EDGE,{"derivedFrom":sQuery(id+"F2.wireOp",EDGE,"E5.0.16.0")}),1.0]])]});
            var Q136;
            Q136=makeQuery(id+"F2.imprint","IMPRINT",FACE,{"disambiguationData":[TD([[makeQuery(id+"F2.imprint","IMPRINT",EDGE,{"derivedFrom":sQuery(id+"F2.wireOp",EDGE,"E5.0.15.0")}),1.0]])]});
            var Q137;
            Q137=makeQuery(id+"F2.imprint","IMPRINT",FACE,{"disambiguationData":[TD([[makeQuery(id+"F2.imprint","IMPRINT",EDGE,{"derivedFrom":sQuery(id+"F2.wireOp",EDGE,"E5.1.15.0")}),1.0]])]});
            var Q138;
            Q138=makeQuery(id+"F2.imprint","IMPRINT",FACE,{"disambiguationData":[TD([[makeQuery(id+"F2.imprint","IMPRINT",EDGE,{"derivedFrom":sQuery(id+"F2.wireOp",EDGE,"E5.1.14.0")}),1.0]])]});
            var Q139;
            Q139=makeQuery(id+"F2.imprint","IMPRINT",FACE,{"disambiguationData":[TD([[makeQuery(id+"F2.imprint","IMPRINT",EDGE,{"derivedFrom":sQuery(id+"F2.wireOp",EDGE,"E5.0.14.0")}),1.0]])]});
            var Q140;
            Q140=makeQuery(id+"F2.imprint","IMPRINT",FACE,{"disambiguationData":[TD([[makeQuery(id+"F2.imprint","IMPRINT",EDGE,{"derivedFrom":sQuery(id+"F2.wireOp",EDGE,"E5.0.13.0")}),1.0]])]});
            var Q141;
            Q141=makeQuery(id+"F2.imprint","IMPRINT",FACE,{"disambiguationData":[TD([[makeQuery(id+"F2.imprint","IMPRINT",EDGE,{"derivedFrom":sQuery(id+"F2.wireOp",EDGE,"E5.1.13.0")}),1.0]])]});
            var Q142;
            Q142=makeQuery(id+"F2.imprint","IMPRINT",FACE,{"disambiguationData":[TD([[makeQuery(id+"F2.imprint","IMPRINT",EDGE,{"derivedFrom":sQuery(id+"F2.wireOp",EDGE,"E5.1.12.0")}),1.0]])]});
            var Q143;
            Q143=makeQuery(id+"F2.imprint","IMPRINT",FACE,{"disambiguationData":[TD([[makeQuery(id+"F2.imprint","IMPRINT",EDGE,{"derivedFrom":sQuery(id+"F2.wireOp",EDGE,"E5.0.12.0")}),1.0]])]});
            var Q144;
            Q144=makeQuery(id+"F2.imprint","IMPRINT",FACE,{"disambiguationData":[TD([[makeQuery(id+"F2.imprint","IMPRINT",EDGE,{"derivedFrom":sQuery(id+"F2.wireOp",EDGE,"E5.0.11.0")}),1.0]])]});
            var Q145;
            Q145=makeQuery(id+"F2.imprint","IMPRINT",FACE,{"disambiguationData":[TD([[makeQuery(id+"F2.imprint","IMPRINT",EDGE,{"derivedFrom":sQuery(id+"F2.wireOp",EDGE,"E5.1.11.0")}),1.0]])]});
            var Q146;
            Q146=makeQuery(id+"F2.imprint","IMPRINT",FACE,{"disambiguationData":[TD([[makeQuery(id+"F2.imprint","IMPRINT",EDGE,{"derivedFrom":sQuery(id+"F2.wireOp",EDGE,"E5.1.10.0")}),1.0]])]});
            var Q147;
            Q147=makeQuery(id+"F2.imprint","IMPRINT",FACE,{"disambiguationData":[TD([[makeQuery(id+"F2.imprint","IMPRINT",EDGE,{"derivedFrom":sQuery(id+"F2.wireOp",EDGE,"E5.0.10.0")}),1.0]])]});
            var Q148;
            Q148=makeQuery(id+"F2.imprint","IMPRINT",FACE,{"disambiguationData":[TD([[makeQuery(id+"F2.imprint","IMPRINT",EDGE,{"derivedFrom":sQuery(id+"F2.wireOp",EDGE,"E5.0.9.0")}),1.0]])]});
            var Q149;
            Q149=makeQuery(id+"F2.imprint","IMPRINT",FACE,{"disambiguationData":[TD([[makeQuery(id+"F2.imprint","IMPRINT",EDGE,{"derivedFrom":sQuery(id+"F2.wireOp",EDGE,"E5.1.9.0")}),1.0]])]});
            var Q150;
            Q150=makeQuery(id+"F2.imprint","IMPRINT",FACE,{"disambiguationData":[TD([[makeQuery(id+"F2.imprint","IMPRINT",EDGE,{"derivedFrom":sQuery(id+"F2.wireOp",EDGE,"E5.1.8.0")}),1.0]])]});
            var Q151;
            Q151=makeQuery(id+"F2.imprint","IMPRINT",FACE,{"disambiguationData":[TD([[makeQuery(id+"F2.imprint","IMPRINT",EDGE,{"derivedFrom":sQuery(id+"F2.wireOp",EDGE,"E5.0.8.0")}),1.0]])]});
            var Q152;
            Q152=makeQuery(id+"F2.imprint","IMPRINT",FACE,{"disambiguationData":[TD([[makeQuery(id+"F2.imprint","IMPRINT",EDGE,{"derivedFrom":sQuery(id+"F2.wireOp",EDGE,"E5.0.7.0")}),1.0]])]});
            var Q153;
            Q153=makeQuery(id+"F2.imprint","IMPRINT",FACE,{"disambiguationData":[TD([[makeQuery(id+"F2.imprint","IMPRINT",EDGE,{"derivedFrom":sQuery(id+"F2.wireOp",EDGE,"E5.1.7.0")}),1.0]])]});
            var Q154;
            Q154=makeQuery(id+"F2.imprint","IMPRINT",FACE,{"disambiguationData":[TD([[makeQuery(id+"F2.imprint","IMPRINT",EDGE,{"derivedFrom":sQuery(id+"F2.wireOp",EDGE,"E5.1.6.0")}),1.0]])]});
            var Q155;
            Q155=makeQuery(id+"F2.imprint","IMPRINT",FACE,{"disambiguationData":[TD([[makeQuery(id+"F2.imprint","IMPRINT",EDGE,{"derivedFrom":sQuery(id+"F2.wireOp",EDGE,"E5.0.6.0")}),1.0]])]});
            var Q156;
            Q156=makeQuery(id+"F2.imprint","IMPRINT",FACE,{"disambiguationData":[TD([[makeQuery(id+"F2.imprint","IMPRINT",EDGE,{"derivedFrom":sQuery(id+"F2.wireOp",EDGE,"E5.0.5.0")}),1.0]])]});
            var Q157;
            Q157=makeQuery(id+"F2.imprint","IMPRINT",FACE,{"disambiguationData":[TD([[makeQuery(id+"F2.imprint","IMPRINT",EDGE,{"derivedFrom":sQuery(id+"F2.wireOp",EDGE,"E5.1.5.0")}),1.0]])]});
            var Q158;
            Q158=makeQuery(id+"F2.imprint","IMPRINT",FACE,{"disambiguationData":[TD([[makeQuery(id+"F2.imprint","IMPRINT",EDGE,{"derivedFrom":sQuery(id+"F2.wireOp",EDGE,"E5.1.4.0")}),1.0]])]});
            var Q159;
            Q159=makeQuery(id+"F2.imprint","IMPRINT",FACE,{"disambiguationData":[TD([[makeQuery(id+"F2.imprint","IMPRINT",EDGE,{"derivedFrom":sQuery(id+"F2.wireOp",EDGE,"E5.0.4.0")}),1.0]])]});
            var Q160;
            Q160=makeQuery(id+"F2.imprint","IMPRINT",FACE,{"disambiguationData":[TD([[makeQuery(id+"F2.imprint","IMPRINT",EDGE,{"derivedFrom":sQuery(id+"F2.wireOp",EDGE,"E5.0.3.0")}),1.0]])]});
            var Q161;
            Q161=makeQuery(id+"F2.imprint","IMPRINT",FACE,{"disambiguationData":[TD([[makeQuery(id+"F2.imprint","IMPRINT",EDGE,{"derivedFrom":sQuery(id+"F2.wireOp",EDGE,"E5.1.3.0")}),1.0]])]});
            var Q162;
            Q162=makeQuery(id+"F2.imprint","IMPRINT",FACE,{"disambiguationData":[TD([[makeQuery(id+"F2.imprint","IMPRINT",EDGE,{"derivedFrom":sQuery(id+"F2.wireOp",EDGE,"E5.1.2.0")}),1.0]])]});
            var Q163;
            Q163=makeQuery(id+"F2.imprint","IMPRINT",FACE,{"disambiguationData":[TD([[makeQuery(id+"F2.imprint","IMPRINT",EDGE,{"derivedFrom":sQuery(id+"F2.wireOp",EDGE,"E5.0.2.0")}),1.0]])]});
            extrude(context, id + "F3", {"entities" : qUnion([Q0, Q1, Q2, Q3, Q4, Q5, Q6, Q7, Q8, Q9, Q10, Q11, Q12, Q13, Q14, Q15, Q16, Q17, Q18, Q19, Q20, Q21, Q22, Q23, Q24, Q25, Q26, Q27, Q28, Q29, Q30, Q31, Q32, Q33, Q34, Q35, Q36, Q37, Q38, Q39, Q40, Q41, Q42, Q43, Q44, Q45, Q46, Q47, Q48, Q49, Q50, Q51, Q52, Q53, Q54, Q55, Q56, Q57, Q58, Q59, Q60, Q61, Q62, Q63, Q64, Q65, Q66, Q67, Q68, Q69, Q70, Q71, Q72, Q73, Q74, Q75, Q76, Q77, Q78, Q79, Q80, Q81, Q82, Q83, Q84, Q85, Q86, Q87, Q88, Q89, Q90, Q91, Q92, Q93, Q94, Q95, Q96, Q97, Q98, Q99, Q100, Q101, Q102, Q103, Q104, Q105, Q106, Q107, Q108, Q109, Q110, Q111, Q112, Q113, Q114, Q115, Q116, Q117, Q118, Q119, Q120, Q121, Q122, Q123, Q124, Q125, Q126, Q127, Q128, Q129, Q130, Q131, Q132, Q133, Q134, Q135, Q136, Q137, Q138, Q139, Q140, Q141, Q142, Q143, Q144, Q145, Q146, Q147, Q148, Q149, Q150, Q151, Q152, Q153, Q154, Q155, Q156, Q157, Q158, Q159, Q160, Q161, Q162, Q163]), "operationType" : NewBodyOperationType.REMOVE, "oppositeDirection" : true, "depth" : 25 * mm});
        }
        {
            var Q0;
            Q0=makeQuery(id+"F1.opExtrude","CAP_FACE",FACE,{"disambiguationData":[OSD([sQuery(id+"F0.wireOp",EDGE,"E0.rect.bottom"),sQuery(id+"F0.wireOp",EDGE,"E0.rect.top"),sQuery(id+"F0.wireOp",EDGE,"E0.rect.left"),sQuery(id+"F0.wireOp",EDGE,"E0.rect.right")])],"isStart":false});
            var sketch = newSketch(context, id + "F4", { "sketchPlane" : qUnion([Q0])});
            skLineSegment(sketch, "E6.rect.bottom", {"start": v(50.8, -63.5) * mm, "end": v(-50.8, -63.5) * mm});
            skLineSegment(sketch, "E6.rect.top", {"start": v(50.8, 63.5) * mm, "end": v(-50.8, 63.5) * mm});
            skLineSegment(sketch, "E6.rect.left", {"start": v(50.8, -63.5) * mm, "end": v(50.8, 63.5) * mm});
            skLineSegment(sketch, "E6.rect.right", {"start": v(-50.8, -63.5) * mm, "end": v(-50.8, 63.5) * mm});
            skPoint(sketch, "E6.rect.middle", {"position": v(0, 0) * mm});
            skCircle(sketch, "E7", {"center": v(-50.8, 63.5) * mm, "radius": 1.5 * mm});
            skCircle(sketch, "E8", {"center": v(50.8, 63.5) * mm, "radius": 1.5 * mm});
            skCircle(sketch, "E9", {"center": v(50.8, -63.5) * mm, "radius": 1.5 * mm});
            skCircle(sketch, "E10", {"center": v(-50.8, -63.5) * mm, "radius": 1.5 * mm});
            skSolve(sketch);
        }
        {
            var Q0;
            {var subQ0=sQuery(id+"F4.wireOp",EDGE,"E6.rect.right");var subQ3=sQuery(id+"F4.wireOp",EDGE,"E6.rect.bottom");var subQ4=makeQuery(id+"F4.imprint","INTERSECT",VERTEX,{"derivedFrom":[subQ3,subQ0]});Q0=makeQuery(id+"F4.imprint","IMPRINT",FACE,{"disambiguationData":[TD([[makeQuery(id+"F4.imprint","IMPRINT",EDGE,{"disambiguationData":[TD([[subQ4,1.0]])],"derivedFrom":subQ3}),1.0]])]});}
            var Q1;
            {var subQ1=sQuery(id+"F4.wireOp",EDGE,"E6.rect.right");var subQ3=sQuery(id+"F4.wireOp",EDGE,"E6.rect.bottom");var subQ5=makeQuery(id+"F4.imprint","INTERSECT",VERTEX,{"derivedFrom":[subQ3,subQ1]});Q1=makeQuery(id+"F4.imprint","IMPRINT",FACE,{"disambiguationData":[TD([[makeQuery(id+"F4.imprint","IMPRINT",EDGE,{"disambiguationData":[TD([[subQ5,1.0]])],"derivedFrom":subQ3}),-1.0]])]});}
            var Q2;
            {var subQ1=sQuery(id+"F4.wireOp",EDGE,"E6.rect.left");var subQ3=sQuery(id+"F4.wireOp",EDGE,"E6.rect.bottom");var subQ5=makeQuery(id+"F4.imprint","INTERSECT",VERTEX,{"derivedFrom":[subQ3,subQ1]});Q2=makeQuery(id+"F4.imprint","IMPRINT",FACE,{"disambiguationData":[TD([[makeQuery(id+"F4.imprint","IMPRINT",EDGE,{"disambiguationData":[TD([[subQ5,-1.0]])],"derivedFrom":subQ3}),1.0]])]});}
            var Q3;
            {var subQ1=sQuery(id+"F4.wireOp",EDGE,"E6.rect.left");var subQ3=sQuery(id+"F4.wireOp",EDGE,"E6.rect.bottom");var subQ5=makeQuery(id+"F4.imprint","INTERSECT",VERTEX,{"derivedFrom":[subQ3,subQ1]});Q3=makeQuery(id+"F4.imprint","IMPRINT",FACE,{"disambiguationData":[TD([[makeQuery(id+"F4.imprint","IMPRINT",EDGE,{"disambiguationData":[TD([[subQ5,-1.0]])],"derivedFrom":subQ3}),-1.0]])]});}
            var Q4;
            {var subQ1=sQuery(id+"F4.wireOp",EDGE,"E6.rect.left");var subQ3=sQuery(id+"F4.wireOp",EDGE,"E6.rect.top");var subQ5=makeQuery(id+"F4.imprint","INTERSECT",VERTEX,{"derivedFrom":[subQ3,subQ1]});Q4=makeQuery(id+"F4.imprint","IMPRINT",FACE,{"disambiguationData":[TD([[makeQuery(id+"F4.imprint","IMPRINT",EDGE,{"disambiguationData":[TD([[subQ5,-1.0]])],"derivedFrom":subQ3}),1.0]])]});}
            var Q5;
            {var subQ1=sQuery(id+"F4.wireOp",EDGE,"E6.rect.left");var subQ3=sQuery(id+"F4.wireOp",EDGE,"E6.rect.top");var subQ5=makeQuery(id+"F4.imprint","INTERSECT",VERTEX,{"derivedFrom":[subQ3,subQ1]});Q5=makeQuery(id+"F4.imprint","IMPRINT",FACE,{"disambiguationData":[TD([[makeQuery(id+"F4.imprint","IMPRINT",EDGE,{"disambiguationData":[TD([[subQ5,-1.0]])],"derivedFrom":subQ3}),-1.0]])]});}
            var Q6;
            {var subQ1=sQuery(id+"F4.wireOp",EDGE,"E6.rect.right");var subQ3=sQuery(id+"F4.wireOp",EDGE,"E6.rect.top");var subQ5=makeQuery(id+"F4.imprint","INTERSECT",VERTEX,{"derivedFrom":[subQ3,subQ1]});Q6=makeQuery(id+"F4.imprint","IMPRINT",FACE,{"disambiguationData":[TD([[makeQuery(id+"F4.imprint","IMPRINT",EDGE,{"disambiguationData":[TD([[subQ5,1.0]])],"derivedFrom":subQ3}),-1.0]])]});}
            var Q7;
            {var subQ1=sQuery(id+"F4.wireOp",EDGE,"E6.rect.right");var subQ3=sQuery(id+"F4.wireOp",EDGE,"E6.rect.top");var subQ5=makeQuery(id+"F4.imprint","INTERSECT",VERTEX,{"derivedFrom":[subQ3,subQ1]});Q7=makeQuery(id+"F4.imprint","IMPRINT",FACE,{"disambiguationData":[TD([[makeQuery(id+"F4.imprint","IMPRINT",EDGE,{"disambiguationData":[TD([[subQ5,1.0]])],"derivedFrom":subQ3}),1.0]])]});}
            extrude(context, id + "F5", {"entities" : qUnion([Q0, Q1, Q2, Q3, Q4, Q5, Q6, Q7]), "operationType" : NewBodyOperationType.REMOVE, "oppositeDirection" : true, "depth" : 25 * mm});
        }
    });
